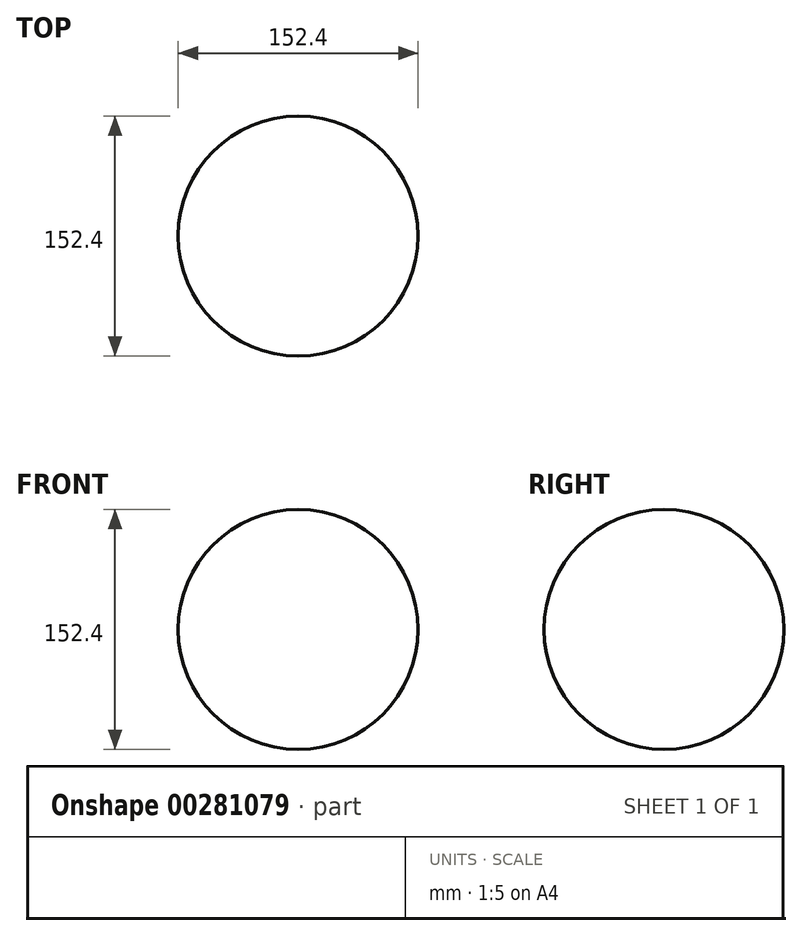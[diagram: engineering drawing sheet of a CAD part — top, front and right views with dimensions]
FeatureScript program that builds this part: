
annotation { "Feature Type Name" : "Feature", "Feature Type Description" : "" }
export const myFeature = defineFeature(function(context is Context, id is Id, definition is map)
    precondition{}
    {
        {
            var Q0;
            Q0=qCreatedBy(makeId("Front.planeOp"),FACE);
            var sketch = newSketch(context, id + "F0", { "sketchPlane" : qUnion([Q0])});
            skLineSegment(sketch, "E0", {"start": v(0, 89.55) * mm, "end": v(0, -88.25) * mm, "construction": true});
            skSolve(sketch);
        }
        {
            var Q0;
            Q0=qCreatedBy(makeId("Front.planeOp"),FACE);
            var sketch = newSketch(context, id + "F1", { "sketchPlane" : qUnion([Q0])});
            skArc(sketch, "E1", {"start": v(0, 76.2) * mm, "mid": v(-76.2, 0) * mm, "end": v(0, -76.2) * mm});
            skSolve(sketch);
        }
        {
            var Q0;
            Q0 = qConstructionFilter(qBodyType(qCreatedBy(id + "F1" ,EDGE), BodyType.WIRE), ConstructionObject.NO);
            var Q1;
            Q1=sQuery(id+"F0.wireOp",EDGE,"E0");
            revolve(context, id + "F2", {"bodyType" : ToolBodyType.SURFACE, "surfaceEntities" : qUnion([Q0]), "axis" : qUnion([Q1]), "revolveType" : RevolveType.FULL});
        }
    });
